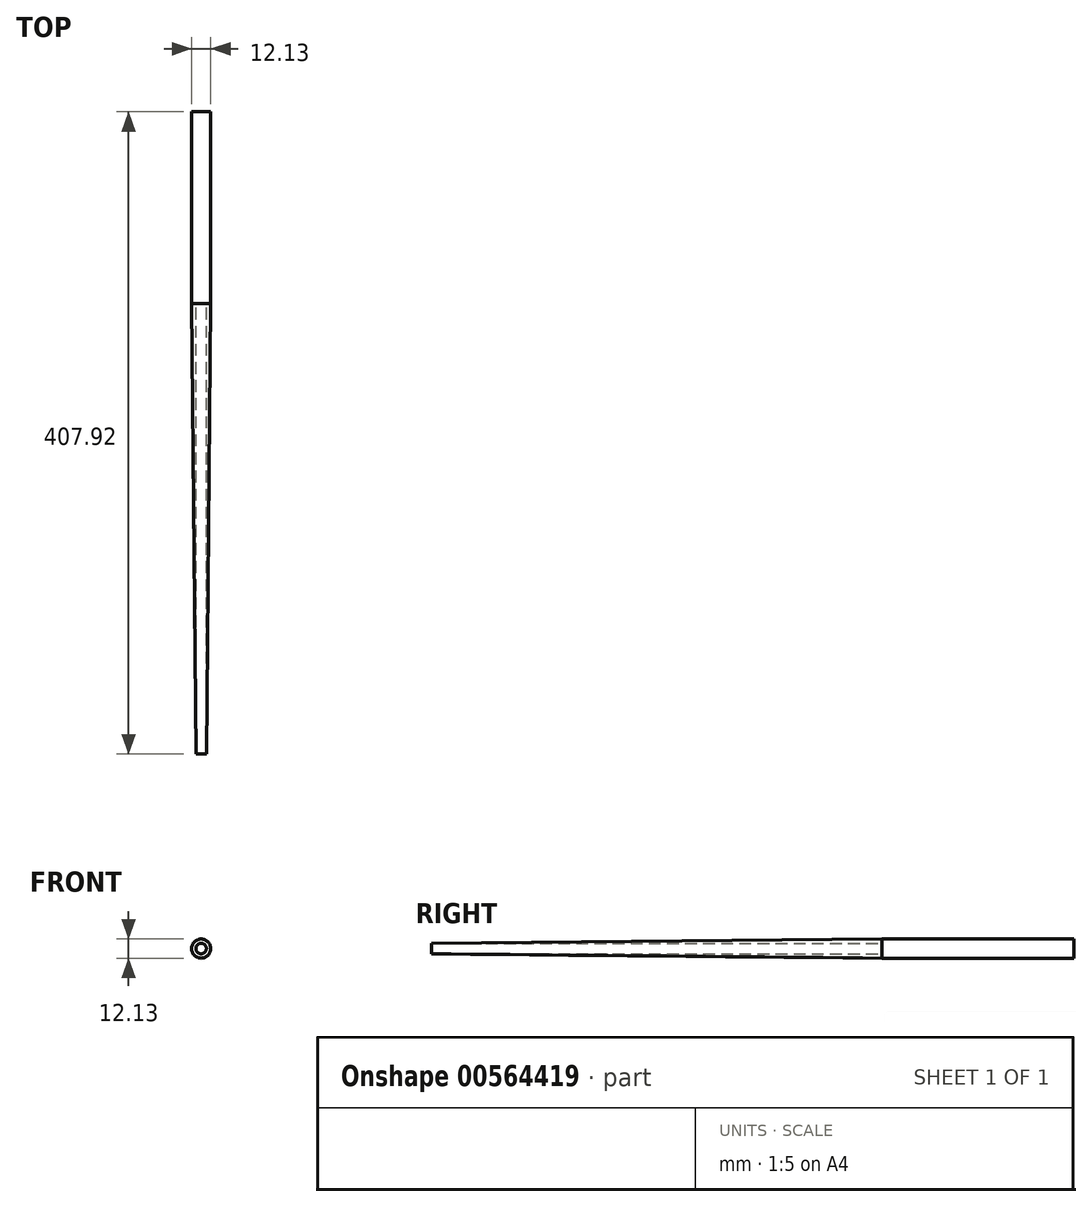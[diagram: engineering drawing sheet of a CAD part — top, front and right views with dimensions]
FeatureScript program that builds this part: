
annotation { "Feature Type Name" : "Feature", "Feature Type Description" : "" }
export const myFeature = defineFeature(function(context is Context, id is Id, definition is map)
    precondition{}
    {
        {
            var Q0;
            Q0=qCreatedBy(makeId("Front.planeOp"),FACE);
            var sketch = newSketch(context, id + "F0", { "sketchPlane" : qUnion([Q0])});
            skCircle(sketch, "E0", {"center": v(-65.38, 30.55) * mm, "radius": 14.22 * mm});
            skSolve(sketch);
        }
        {
            var Q0;
            Q0=makeQuery(id+"F0.imprint","IMPRINT",FACE,{"disambiguationData":[TD([[makeQuery(id+"F0.imprint","IMPRINT",EDGE,{"derivedFrom":sQuery(id+"F0.wireOp",EDGE,"E0")}),1.0]])]});
            var sketch = newSketch(context, id + "F1", { "sketchPlane" : qUnion([Q0])});
            skCircle(sketch, "E1", {"center": v(-65.24, 30.75) * mm, "radius": 6.06 * mm});
            skSolve(sketch);
        }
        {
            var Q0;
            Q0=makeQuery(id+"F1.imprint","IMPRINT",FACE,{"disambiguationData":[TD([[makeQuery(id+"F1.imprint","IMPRINT",EDGE,{"derivedFrom":sQuery(id+"F1.wireOp",EDGE,"E1")}),1.0]])]});
            var Q1;
            Q1=sQuery(id+"F1.wireOp",EDGE,"E1");
            extrude(context, id + "F2", {"entities" : qUnion([Q0]), "surfaceEntities" : qUnion([Q1]), "depth" : 121.92 * mm, "offsetDistance" : 25.4 * mm});
        }
        {
            var Q0;
            Q0=makeQuery(id+"F2.opExtrude","CAP_FACE",FACE,{"disambiguationData":[OSD([sQuery(id+"F1.wireOp",EDGE,"E1")])],"isStart":false});
            var sketch = newSketch(context, id + "F3", { "sketchPlane" : qUnion([Q0])});
            skCircle(sketch, "E2", {"center": v(-65.24, 30.75) * mm, "radius": 3.34 * mm});
            skSolve(sketch);
        }
        {
            var Q0;
            Q0=makeQuery(id+"F3.imprint","IMPRINT",FACE,{"disambiguationData":[TD([[makeQuery(id+"F3.imprint","IMPRINT",EDGE,{"derivedFrom":sQuery(id+"F3.wireOp",EDGE,"E2")}),1.0]])]});
            var Q1;
            Q1=sQuery(id+"F3.wireOp",EDGE,"E2");
            extrude(context, id + "F4", {"entities" : qUnion([Q0]), "surfaceEntities" : qUnion([Q1]), "depth" : 286 * mm, "offsetDistance" : 25.4 * mm});
        }
        {
            var Q0;
            Q0=makeQuery(id+"F2.opExtrude","CAP_FACE",FACE,{"disambiguationData":[OSD([sQuery(id+"F1.wireOp",EDGE,"E1")])],"isStart":false});
            var Q1;
            Q1=makeQuery(id+"F4.opExtrude","CAP_FACE",FACE,{"disambiguationData":[OSD([sQuery(id+"F3.wireOp",EDGE,"E2")])],"isStart":false});
            loft(context, id + "F5", {"sheetProfilesArray" : [{ "sheetProfileEntities" : qUnion([Q0]) }, { "sheetProfileEntities" : qUnion([Q1]) }]});
        }
    });
